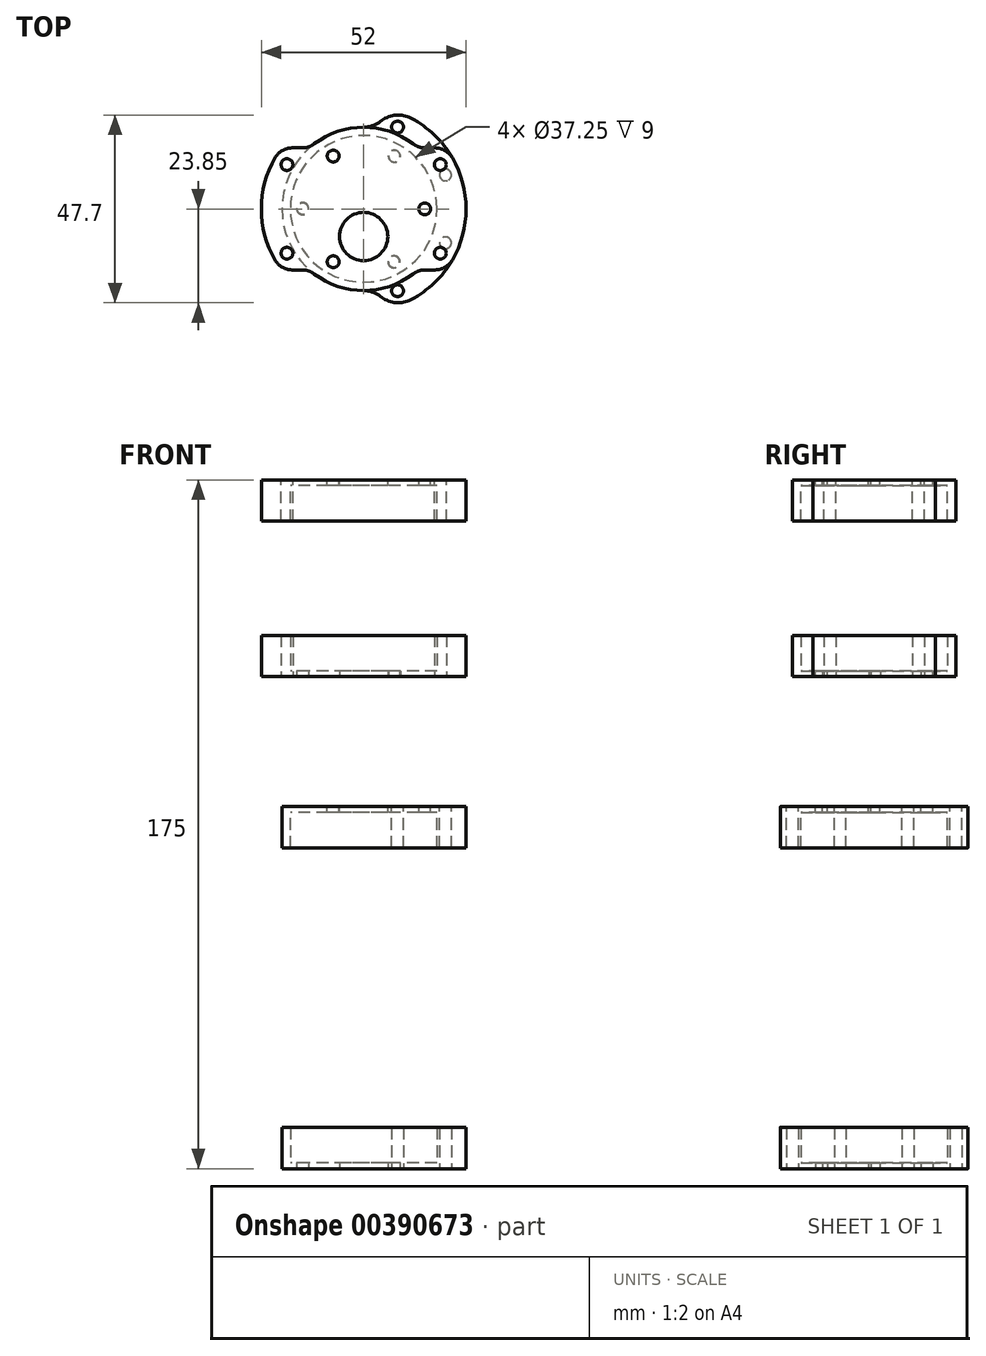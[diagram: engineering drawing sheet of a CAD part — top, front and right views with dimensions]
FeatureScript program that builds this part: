
annotation { "Feature Type Name" : "Feature", "Feature Type Description" : "" }
export const myFeature = defineFeature(function(context is Context, id is Id, definition is map)
    precondition{}
    {
        {
            var Q0;
            Q0=qCreatedBy(makeId("Top.planeOp"),FACE);
            cPlane(context, id + "F0", {"entities" : qUnion([Q0]), "cplaneType" : CPlaneType.OFFSET, "offset" : 92 * mm, "width" : 150 * mm, "height" : 150 * mm});
        }
        {
            var Q0;
            Q0=qCreatedBy(makeId("Top.planeOp"),FACE);
            var sketch = newSketch(context, id + "F1", { "sketchPlane" : qUnion([Q0])});
            skCircle(sketch, "E0", {"center": v(0, 0) * mm, "radius": 18.62 * mm});
            skCircle(sketch, "E1", {"center": v(0, 0) * mm, "radius": 26 * mm});
            skCircle(sketch, "E2", {"center": v(0, -7) * mm, "radius": 6.12 * mm});
            skCircle(sketch, "E3", {"center": v(0, 0) * mm, "radius": 15.5 * mm, "construction": true});
            skCircle(sketch, "E4", {"center": v(-15.5, 0) * mm, "radius": 1.5 * mm});
            skCircle(sketch, "E5.1.0", {"center": v(7.75, -13.42) * mm, "radius": 1.5 * mm});
            skCircle(sketch, "E5.2.0", {"center": v(7.75, 13.42) * mm, "radius": 1.5 * mm});
            skCircle(sketch, "E6", {"center": v(-20.79, 8.61) * mm, "radius": 1.5 * mm});
            skLineSegment(sketch, "E7", {"start": v(-20.79, 8.61) * mm, "end": v(0, 0) * mm, "construction": true});
            skCircle(sketch, "E8.1.0", {"center": v(-20.79, -8.61) * mm, "radius": 1.5 * mm});
            skCircle(sketch, "E8.2.0", {"center": v(-8.61, -20.79) * mm, "radius": 1.5 * mm});
            skCircle(sketch, "E8.3.0", {"center": v(8.61, -20.79) * mm, "radius": 1.5 * mm});
            skCircle(sketch, "E8.4.0", {"center": v(20.79, -8.61) * mm, "radius": 1.5 * mm});
            skCircle(sketch, "E8.5.0", {"center": v(20.79, 8.61) * mm, "radius": 1.5 * mm});
            skCircle(sketch, "E9", {"center": v(0, 0) * mm, "radius": 20.75 * mm});
            skLineSegment(sketch, "E10", {"start": v(0, 20.75) * mm, "end": v(0, 26) * mm});
            skLineSegment(sketch, "E11", {"start": v(0, -20.75) * mm, "end": v(0, -26) * mm});
            skCircle(sketch, "E12.1.6.0", {"center": v(8.61, 20.79) * mm, "radius": 1.5 * mm});
            skCircle(sketch, "E12.1.7.0", {"center": v(-8.61, 20.79) * mm, "radius": 1.5 * mm});
            skSolve(sketch);
        }
        {
            var Q0;
            Q0=qCreatedBy(id+"F0.planeOp",FACE);
            var sketch = newSketch(context, id + "F2", { "sketchPlane" : qUnion([Q0])});
            skCircle(sketch, "E13", {"center": v(0, 0) * mm, "radius": 18.62 * mm});
            skCircle(sketch, "E14", {"center": v(0, 0) * mm, "radius": 26 * mm});
            skCircle(sketch, "E15", {"center": v(0, -7) * mm, "radius": 6.12 * mm});
            skCircle(sketch, "E16", {"center": v(0, 0) * mm, "radius": 15.5 * mm, "construction": true});
            skCircle(sketch, "E17", {"center": v(-20.79, 8.61) * mm, "radius": 1.5 * mm});
            skLineSegment(sketch, "E18", {"start": v(-20.79, 8.61) * mm, "end": v(0, 0) * mm, "construction": true});
            skCircle(sketch, "E19.1.0", {"center": v(-20.79, -8.61) * mm, "radius": 1.5 * mm});
            skCircle(sketch, "E19.2.0", {"center": v(-8.61, -20.79) * mm, "radius": 1.5 * mm});
            skCircle(sketch, "E19.3.0", {"center": v(8.61, -20.79) * mm, "radius": 1.5 * mm});
            skCircle(sketch, "E19.4.0", {"center": v(20.79, -8.61) * mm, "radius": 1.5 * mm});
            skCircle(sketch, "E19.5.0", {"center": v(20.79, 8.61) * mm, "radius": 1.5 * mm});
            skCircle(sketch, "E20", {"center": v(0, 0) * mm, "radius": 20.75 * mm});
            skLineSegment(sketch, "E21", {"start": v(0, 20.75) * mm, "end": v(0, 26) * mm});
            skLineSegment(sketch, "E22", {"start": v(0, -20.75) * mm, "end": v(0, -26) * mm});
            skCircle(sketch, "E23.1.6.0", {"center": v(8.61, 20.79) * mm, "radius": 1.5 * mm});
            skCircle(sketch, "E23.1.7.0", {"center": v(-8.61, 20.79) * mm, "radius": 1.5 * mm});
            skCircle(sketch, "E24", {"center": v(15.5, 0) * mm, "radius": 1.5 * mm});
            skCircle(sketch, "E25.1.0", {"center": v(-7.75, 13.42) * mm, "radius": 1.5 * mm});
            skCircle(sketch, "E25.2.0", {"center": v(-7.75, -13.42) * mm, "radius": 1.5 * mm});
            skSolve(sketch);
        }
        {
            var Q0;
            Q0=makeQuery(id+"F1.imprint","IMPRINT",FACE,{"disambiguationData":[TD([[makeQuery(id+"F1.imprint","IMPRINT",EDGE,{"derivedFrom":sQuery(id+"F1.wireOp",EDGE,"E0")}),1.0]])]});
            extrude(context, id + "F3", {"entities" : qUnion([Q0]), "depth" : 1.5 * mm});
        }
        {
            var Q0;
            Q0=makeQuery(id+"F2.imprint","IMPRINT",FACE,{"disambiguationData":[TD([[makeQuery(id+"F2.imprint","IMPRINT",EDGE,{"derivedFrom":sQuery(id+"F2.wireOp",EDGE,"E13")}),1.0]])]});
            extrude(context, id + "F4", {"entities" : qUnion([Q0]), "oppositeDirection" : true, "depth" : 1.5 * mm});
        }
        {
            var Q0;
            Q0=makeQuery(id+"F1.imprint","IMPRINT",FACE,{"disambiguationData":[TD([[makeQuery(id+"F1.imprint","IMPRINT",EDGE,{"derivedFrom":sQuery(id+"F1.wireOp",EDGE,"E0")}),-1.0]])]});
            var Q1;
            Q1=makeQuery(id+"F1.imprint","IMPRINT",FACE,{"disambiguationData":[TD([[makeQuery(id+"F1.imprint","IMPRINT",EDGE,{"derivedFrom":sQuery(id+"F1.wireOp",EDGE,"E8.3.0")}),-1.0]])]});
            extrude(context, id + "F5", {"entities" : qUnion([Q0, Q1]), "operationType" : NewBodyOperationType.ADD, "depth" : 10.5 * mm});
        }
        {
            var Q0;
            Q0=makeQuery(id+"F2.imprint","IMPRINT",FACE,{"disambiguationData":[TD([[makeQuery(id+"F2.imprint","IMPRINT",EDGE,{"derivedFrom":sQuery(id+"F2.wireOp",EDGE,"E13")}),-1.0]])]});
            var Q1;
            Q1=makeQuery(id+"F2.imprint","IMPRINT",FACE,{"disambiguationData":[TD([[makeQuery(id+"F2.imprint","IMPRINT",EDGE,{"derivedFrom":sQuery(id+"F2.wireOp",EDGE,"E19.3.0")}),-1.0]])]});
            extrude(context, id + "F6", {"entities" : qUnion([Q0, Q1]), "operationType" : NewBodyOperationType.ADD, "oppositeDirection" : true, "depth" : 10.5 * mm});
        }
        {
            var Q0;
            Q0=makeQuery(id+"F5.opExtrude","SWEPT_EDGE",EDGE,{"disambiguationData":[OSD([sQuery(id+"F1.wireOp",EDGE,"E1"),sQuery(id+"F1.wireOp",EDGE,"E10")])]});
            var Q1;
            Q1=makeQuery(id+"F5.opExtrude","SWEPT_EDGE",EDGE,{"disambiguationData":[OSD([sQuery(id+"F1.wireOp",EDGE,"E1"),sQuery(id+"F1.wireOp",EDGE,"E11")])]});
            var Q2;
            Q2=makeQuery(id+"F5.opExtrude","SWEPT_EDGE",EDGE,{"disambiguationData":[OSD([sQuery(id+"F2.wireOp",EDGE,"E14"),sQuery(id+"F2.wireOp",EDGE,"E22")])]});
            var Q3;
            Q3=makeQuery(id+"F5.opExtrude","SWEPT_EDGE",EDGE,{"disambiguationData":[OSD([sQuery(id+"F2.wireOp",EDGE,"E14"),sQuery(id+"F2.wireOp",EDGE,"E21")])]});
            var Q4;
            Q4=makeQuery(id+"F6.opExtrude","SWEPT_EDGE",EDGE,{"disambiguationData":[OSD([sQuery(id+"F2.wireOp",EDGE,"E14"),sQuery(id+"F2.wireOp",EDGE,"E21")])]});
            var Q5;
            Q5=makeQuery(id+"F6.opExtrude","SWEPT_EDGE",EDGE,{"disambiguationData":[OSD([sQuery(id+"F2.wireOp",EDGE,"E14"),sQuery(id+"F2.wireOp",EDGE,"E22")])]});
            chamfer(context, id + "F7", {"entities" : qUnion([Q0, Q1, Q2, Q3, Q4, Q5]), "width" : 6 * mm, "tangentPropagation" : true});
        }
        {
            var Q0;
            Q0=makeQuery(id+"F7.opChamfer","BLEND_EDGE",EDGE,{"blendedFrom":[makeQuery(id+"F5.opExtrude","SWEPT_EDGE",EDGE,{"disambiguationData":[OSD([sQuery(id+"F1.wireOp",EDGE,"E1"),sQuery(id+"F1.wireOp",EDGE,"E11")])]}),makeQuery(id+"F5.opExtrude","SWEPT_FACE",FACE,{"disambiguationData":[OSD([sQuery(id+"F1.wireOp",EDGE,"E9")])]})],"blendedInto":[makeQuery(id+"F5.opExtrude","SWEPT_FACE",FACE,{"disambiguationData":[OSD([sQuery(id+"F1.wireOp",EDGE,"E9")])]})]});
            var Q1;
            Q1=makeQuery(id+"F7.opChamfer","BLEND_EDGE",EDGE,{"blendedFrom":[makeQuery(id+"F5.opExtrude","SWEPT_EDGE",EDGE,{"disambiguationData":[OSD([sQuery(id+"F1.wireOp",EDGE,"E1"),sQuery(id+"F1.wireOp",EDGE,"E10")])]}),makeQuery(id+"F5.opExtrude","SWEPT_FACE",FACE,{"disambiguationData":[OSD([sQuery(id+"F1.wireOp",EDGE,"E9")])]})],"blendedInto":[makeQuery(id+"F5.opExtrude","SWEPT_FACE",FACE,{"disambiguationData":[OSD([sQuery(id+"F1.wireOp",EDGE,"E9")])]})]});
            var Q2;
            {var subQ0=sQuery(id+"F1.wireOp",EDGE,"E1");Q2=makeQuery(id+"F7.opChamfer","BLEND_EDGE",EDGE,{"blendedFrom":[makeQuery(id+"F5.opExtrude","SWEPT_EDGE",EDGE,{"disambiguationData":[OSD([subQ0,sQuery(id+"F1.wireOp",EDGE,"E10")])]}),makeQuery(id+"F5.opExtrude","SWEPT_FACE",FACE,{"disambiguationData":[OSD([subQ0])]})],"blendedInto":[makeQuery(id+"F5.opExtrude","SWEPT_FACE",FACE,{"disambiguationData":[OSD([subQ0])]})]});}
            var Q3;
            {var subQ0=sQuery(id+"F1.wireOp",EDGE,"E1");Q3=makeQuery(id+"F7.opChamfer","BLEND_EDGE",EDGE,{"blendedFrom":[makeQuery(id+"F5.opExtrude","SWEPT_EDGE",EDGE,{"disambiguationData":[OSD([subQ0,sQuery(id+"F1.wireOp",EDGE,"E11")])]}),makeQuery(id+"F5.opExtrude","SWEPT_FACE",FACE,{"disambiguationData":[OSD([subQ0])]})],"blendedInto":[makeQuery(id+"F5.opExtrude","SWEPT_FACE",FACE,{"disambiguationData":[OSD([subQ0])]})]});}
            var Q4;
            {var subQ0=sQuery(id+"F2.wireOp",EDGE,"E14");Q4=makeQuery(id+"F7.opChamfer","BLEND_EDGE",EDGE,{"blendedFrom":[makeQuery(id+"F5.opExtrude","SWEPT_EDGE",EDGE,{"disambiguationData":[OSD([subQ0,sQuery(id+"F2.wireOp",EDGE,"E21")])]}),makeQuery(id+"F5.opExtrude","SWEPT_FACE",FACE,{"disambiguationData":[OSD([subQ0])]})],"blendedInto":[makeQuery(id+"F5.opExtrude","SWEPT_FACE",FACE,{"disambiguationData":[OSD([subQ0])]})]});}
            var Q5;
            Q5=makeQuery(id+"F7.opChamfer","BLEND_EDGE",EDGE,{"blendedFrom":[makeQuery(id+"F5.opExtrude","SWEPT_EDGE",EDGE,{"disambiguationData":[OSD([sQuery(id+"F2.wireOp",EDGE,"E14"),sQuery(id+"F2.wireOp",EDGE,"E21")])]}),makeQuery(id+"F5.opExtrude","SWEPT_FACE",FACE,{"disambiguationData":[OSD([sQuery(id+"F2.wireOp",EDGE,"E20")])]})],"blendedInto":[makeQuery(id+"F5.opExtrude","SWEPT_FACE",FACE,{"disambiguationData":[OSD([sQuery(id+"F2.wireOp",EDGE,"E20")])]})]});
            var Q6;
            Q6=makeQuery(id+"F7.opChamfer","BLEND_EDGE",EDGE,{"blendedFrom":[makeQuery(id+"F5.opExtrude","SWEPT_EDGE",EDGE,{"disambiguationData":[OSD([sQuery(id+"F2.wireOp",EDGE,"E14"),sQuery(id+"F2.wireOp",EDGE,"E22")])]}),makeQuery(id+"F5.opExtrude","SWEPT_FACE",FACE,{"disambiguationData":[OSD([sQuery(id+"F2.wireOp",EDGE,"E20")])]})],"blendedInto":[makeQuery(id+"F5.opExtrude","SWEPT_FACE",FACE,{"disambiguationData":[OSD([sQuery(id+"F2.wireOp",EDGE,"E20")])]})]});
            var Q7;
            {var subQ0=sQuery(id+"F2.wireOp",EDGE,"E14");Q7=makeQuery(id+"F7.opChamfer","BLEND_EDGE",EDGE,{"blendedFrom":[makeQuery(id+"F5.opExtrude","SWEPT_EDGE",EDGE,{"disambiguationData":[OSD([subQ0,sQuery(id+"F2.wireOp",EDGE,"E22")])]}),makeQuery(id+"F5.opExtrude","SWEPT_FACE",FACE,{"disambiguationData":[OSD([subQ0])]})],"blendedInto":[makeQuery(id+"F5.opExtrude","SWEPT_FACE",FACE,{"disambiguationData":[OSD([subQ0])]})]});}
            var Q8;
            {var subQ0=sQuery(id+"F2.wireOp",EDGE,"E14");Q8=makeQuery(id+"F7.opChamfer","BLEND_EDGE",EDGE,{"blendedFrom":[makeQuery(id+"F6.opExtrude","SWEPT_EDGE",EDGE,{"disambiguationData":[OSD([subQ0,sQuery(id+"F2.wireOp",EDGE,"E22")])]}),makeQuery(id+"F6.opExtrude","SWEPT_FACE",FACE,{"disambiguationData":[OSD([subQ0])]})],"blendedInto":[makeQuery(id+"F6.opExtrude","SWEPT_FACE",FACE,{"disambiguationData":[OSD([subQ0])]})]});}
            var Q9;
            Q9=makeQuery(id+"F7.opChamfer","BLEND_EDGE",EDGE,{"blendedFrom":[makeQuery(id+"F6.opExtrude","SWEPT_EDGE",EDGE,{"disambiguationData":[OSD([sQuery(id+"F2.wireOp",EDGE,"E14"),sQuery(id+"F2.wireOp",EDGE,"E22")])]}),makeQuery(id+"F6.opExtrude","SWEPT_FACE",FACE,{"disambiguationData":[OSD([sQuery(id+"F2.wireOp",EDGE,"E20")])]})],"blendedInto":[makeQuery(id+"F6.opExtrude","SWEPT_FACE",FACE,{"disambiguationData":[OSD([sQuery(id+"F2.wireOp",EDGE,"E20")])]})]});
            var Q10;
            Q10=makeQuery(id+"F7.opChamfer","BLEND_EDGE",EDGE,{"blendedFrom":[makeQuery(id+"F6.opExtrude","SWEPT_EDGE",EDGE,{"disambiguationData":[OSD([sQuery(id+"F2.wireOp",EDGE,"E14"),sQuery(id+"F2.wireOp",EDGE,"E21")])]}),makeQuery(id+"F6.opExtrude","SWEPT_FACE",FACE,{"disambiguationData":[OSD([sQuery(id+"F2.wireOp",EDGE,"E20")])]})],"blendedInto":[makeQuery(id+"F6.opExtrude","SWEPT_FACE",FACE,{"disambiguationData":[OSD([sQuery(id+"F2.wireOp",EDGE,"E20")])]})]});
            var Q11;
            {var subQ0=sQuery(id+"F2.wireOp",EDGE,"E14");Q11=makeQuery(id+"F7.opChamfer","BLEND_EDGE",EDGE,{"blendedFrom":[makeQuery(id+"F6.opExtrude","SWEPT_EDGE",EDGE,{"disambiguationData":[OSD([subQ0,sQuery(id+"F2.wireOp",EDGE,"E21")])]}),makeQuery(id+"F6.opExtrude","SWEPT_FACE",FACE,{"disambiguationData":[OSD([subQ0])]})],"blendedInto":[makeQuery(id+"F6.opExtrude","SWEPT_FACE",FACE,{"disambiguationData":[OSD([subQ0])]})]});}
            fillet(context, id + "F8", {"entities" : qUnion([Q0, Q1, Q2, Q3, Q4, Q5, Q6, Q7, Q8, Q9, Q10, Q11]), "radius" : 7 * mm, "tangentPropagation" : true, "allowEdgeOverflow" : false});
        }
        {
            var Q0;
            Q0=qCreatedBy(makeId("Top.planeOp"),FACE);
            cPlane(context, id + "F9", {"entities" : qUnion([Q0]), "cplaneType" : CPlaneType.OFFSET, "offset" : 125 * mm, "width" : 150 * mm, "height" : 150 * mm});
        }
        {
            var Q0;
            Q0=qCreatedBy(id+"F9.planeOp",FACE);
            cPlane(context, id + "F10", {"entities" : qUnion([Q0]), "cplaneType" : CPlaneType.OFFSET, "offset" : 50 * mm, "width" : 150 * mm, "height" : 150 * mm});
        }
        {
            var Q0;
            Q0=qCreatedBy(id+"F9.planeOp",FACE);
            var sketch = newSketch(context, id + "F11", { "sketchPlane" : qUnion([Q0])});
            skCircle(sketch, "E26", {"center": v(0, 0) * mm, "radius": 18.62 * mm});
            skCircle(sketch, "E27", {"center": v(0, 0) * mm, "radius": 26 * mm});
            skCircle(sketch, "E28", {"center": v(0, -7) * mm, "radius": 6.12 * mm});
            skCircle(sketch, "E29", {"center": v(0, 0) * mm, "radius": 15.5 * mm, "construction": true});
            skCircle(sketch, "E30", {"center": v(-15.5, 0.12) * mm, "radius": 1.5 * mm});
            skCircle(sketch, "E31.1.0", {"center": v(7.65, -13.48) * mm, "radius": 1.5 * mm});
            skCircle(sketch, "E31.2.0", {"center": v(7.85, 13.36) * mm, "radius": 1.5 * mm});
            skCircle(sketch, "E32", {"center": v(-19.49, 11.25) * mm, "radius": 1.5 * mm});
            skLineSegment(sketch, "E33", {"start": v(-19.49, 11.25) * mm, "end": v(0, 0) * mm, "construction": true});
            skCircle(sketch, "E34.1.0", {"center": v(-19.49, -11.25) * mm, "radius": 1.5 * mm});
            skCircle(sketch, "E34.2.0", {"center": v(0, -22.5) * mm, "radius": 1.5 * mm});
            skCircle(sketch, "E34.3.0", {"center": v(19.49, -11.25) * mm, "radius": 1.5 * mm});
            skCircle(sketch, "E34.4.0", {"center": v(19.49, 11.25) * mm, "radius": 1.5 * mm});
            skCircle(sketch, "E34.5.0", {"center": v(0, 22.5) * mm, "radius": 1.5 * mm});
            skCircle(sketch, "E35", {"center": v(0, 0) * mm, "radius": 20.75 * mm});
            skLineSegment(sketch, "E36", {"start": v(20.87, -15.5) * mm, "end": v(13.8, -15.5) * mm});
            skLineSegment(sketch, "E37.MirrorCS", {"start": v(-20.87, -15.5) * mm, "end": v(-13.8, -15.5) * mm});
            skLineSegment(sketch, "E38.MirrorCS", {"start": v(20.87, 15.5) * mm, "end": v(13.8, 15.5) * mm});
            skLineSegment(sketch, "E39.MirrorCS", {"start": v(-20.87, 15.5) * mm, "end": v(-13.8, 15.5) * mm});
            skSolve(sketch);
        }
        {
            var Q0;
            Q0=qCreatedBy(id+"F10.planeOp",FACE);
            var sketch = newSketch(context, id + "F12", { "sketchPlane" : qUnion([Q0])});
            skCircle(sketch, "E40", {"center": v(0, 0) * mm, "radius": 18.62 * mm});
            skCircle(sketch, "E41", {"center": v(0, 0) * mm, "radius": 26 * mm});
            skCircle(sketch, "E42", {"center": v(0, -7) * mm, "radius": 6.12 * mm});
            skCircle(sketch, "E43", {"center": v(0, 0) * mm, "radius": 15.5 * mm, "construction": true});
            skCircle(sketch, "E44", {"center": v(0, 0) * mm, "radius": 20.75 * mm});
            skLineSegment(sketch, "E45", {"start": v(20.87, -15.5) * mm, "end": v(13.8, -15.5) * mm});
            skLineSegment(sketch, "E46.MirrorCS", {"start": v(-20.87, -15.5) * mm, "end": v(-13.8, -15.5) * mm});
            skLineSegment(sketch, "E47.MirrorCS", {"start": v(-20.87, 15.5) * mm, "end": v(-13.8, 15.5) * mm});
            skLineSegment(sketch, "E48.MirrorCS", {"start": v(20.87, 15.5) * mm, "end": v(13.8, 15.5) * mm});
            skCircle(sketch, "E49", {"center": v(15.5, 0) * mm, "radius": 1.5 * mm});
            skCircle(sketch, "E50.1.0", {"center": v(-7.75, 13.42) * mm, "radius": 1.5 * mm});
            skCircle(sketch, "E50.2.0", {"center": v(-7.75, -13.42) * mm, "radius": 1.5 * mm});
            skCircle(sketch, "E51", {"center": v(-19.49, 11.25) * mm, "radius": 1.5 * mm});
            skLineSegment(sketch, "E52", {"start": v(-19.49, 11.25) * mm, "end": v(0, 0) * mm, "construction": true});
            skCircle(sketch, "E53.1.0", {"center": v(-19.49, -11.25) * mm, "radius": 1.5 * mm});
            skCircle(sketch, "E53.2.0", {"center": v(0, -22.5) * mm, "radius": 1.5 * mm});
            skCircle(sketch, "E53.3.0", {"center": v(19.49, -11.25) * mm, "radius": 1.5 * mm});
            skCircle(sketch, "E53.4.0", {"center": v(19.49, 11.25) * mm, "radius": 1.5 * mm});
            skCircle(sketch, "E53.5.0", {"center": v(0, 22.5) * mm, "radius": 1.5 * mm});
            skSolve(sketch);
        }
        {
            var Q0;
            Q0=makeQuery(id+"F11.imprint","IMPRINT",FACE,{"disambiguationData":[TD([[makeQuery(id+"F11.imprint","IMPRINT",EDGE,{"derivedFrom":sQuery(id+"F11.wireOp",EDGE,"E26")}),1.0]])]});
            extrude(context, id + "F13", {"entities" : qUnion([Q0]), "depth" : 1.5 * mm});
        }
        {
            var Q0;
            Q0=makeQuery(id+"F11.imprint","IMPRINT",FACE,{"disambiguationData":[TD([[makeQuery(id+"F11.imprint","IMPRINT",EDGE,{"derivedFrom":sQuery(id+"F11.wireOp",EDGE,"E32")}),-1.0]])]});
            var Q1;
            Q1=makeQuery(id+"F11.imprint","IMPRINT",FACE,{"disambiguationData":[TD([[makeQuery(id+"F11.imprint","IMPRINT",EDGE,{"derivedFrom":sQuery(id+"F11.wireOp",EDGE,"E26")}),-1.0]])]});
            var Q2;
            Q2=makeQuery(id+"F11.imprint","IMPRINT",FACE,{"disambiguationData":[TD([[makeQuery(id+"F11.imprint","IMPRINT",EDGE,{"derivedFrom":sQuery(id+"F11.wireOp",EDGE,"E34.3.0")}),-1.0]])]});
            extrude(context, id + "F14", {"entities" : qUnion([Q0, Q1, Q2]), "operationType" : NewBodyOperationType.ADD, "depth" : 10.5 * mm});
        }
        {
            var Q0;
            Q0=makeQuery(id+"F12.imprint","IMPRINT",FACE,{"disambiguationData":[TD([[makeQuery(id+"F12.imprint","IMPRINT",EDGE,{"derivedFrom":sQuery(id+"F12.wireOp",EDGE,"E40")}),1.0]])]});
            extrude(context, id + "F15", {"entities" : qUnion([Q0]), "oppositeDirection" : true, "depth" : 1.5 * mm});
        }
        {
            var Q0;
            {var subQ1=sQuery(id+"F12.wireOp",EDGE,"E45");Q0=makeQuery(id+"F12.imprint","IMPRINT",FACE,{"disambiguationData":[TD([[makeQuery(id+"F12.imprint","IMPRINT",EDGE,{"derivedFrom":subQ1}),-1.0]])]});}
            var Q1;
            Q1=makeQuery(id+"F12.imprint","IMPRINT",FACE,{"disambiguationData":[TD([[makeQuery(id+"F12.imprint","IMPRINT",EDGE,{"derivedFrom":sQuery(id+"F12.wireOp",EDGE,"E40")}),-1.0]])]});
            var Q2;
            {var subQ0=sQuery(id+"F12.wireOp",EDGE,"E46.MirrorCS");Q2=makeQuery(id+"F12.imprint","IMPRINT",FACE,{"disambiguationData":[TD([[makeQuery(id+"F12.imprint","IMPRINT",EDGE,{"derivedFrom":subQ0}),1.0]])]});}
            extrude(context, id + "F16", {"entities" : qUnion([Q0, Q1, Q2]), "operationType" : NewBodyOperationType.ADD, "oppositeDirection" : true, "depth" : 10.5 * mm});
        }
        {
            var Q0;
            Q0=makeQuery(id+"F14.opExtrude","SWEPT_EDGE",EDGE,{"disambiguationData":[OSD([sQuery(id+"F11.wireOp",EDGE,"E27"),sQuery(id+"F11.wireOp",EDGE,"EbLUmnxA-kGfZ-o2ID-BWPR-tWaErnmTWbPK")])]});
            var Q1;
            Q1=makeQuery(id+"F14.opExtrude","SWEPT_EDGE",EDGE,{"disambiguationData":[OSD([sQuery(id+"F11.wireOp",EDGE,"E35"),sQuery(id+"F11.wireOp",EDGE,"EbLUmnxA-kGfZ-o2ID-BWPR-tWaErnmTWbPK")])]});
            var Q2;
            Q2=makeQuery(id+"F14.opExtrude","SWEPT_EDGE",EDGE,{"disambiguationData":[OSD([sQuery(id+"F11.wireOp",EDGE,"E27"),sQuery(id+"F11.wireOp",EDGE,"KzaSrYpL-XU7z-rx1D-WPNd-F9J1fatBlVJU")])]});
            var Q3;
            Q3=makeQuery(id+"F14.opExtrude","SWEPT_EDGE",EDGE,{"disambiguationData":[OSD([sQuery(id+"F11.wireOp",EDGE,"E35"),sQuery(id+"F11.wireOp",EDGE,"KzaSrYpL-XU7z-rx1D-WPNd-F9J1fatBlVJU")])]});
            var Q4;
            Q4=makeQuery(id+"F16.opExtrude","SWEPT_EDGE",EDGE,{"disambiguationData":[OSD([sQuery(id+"F12.wireOp",EDGE,"E44"),sQuery(id+"F12.wireOp",EDGE,"E47.MirrorCS")])]});
            var Q5;
            Q5=makeQuery(id+"F16.opExtrude","SWEPT_EDGE",EDGE,{"disambiguationData":[OSD([sQuery(id+"F12.wireOp",EDGE,"E41"),sQuery(id+"F12.wireOp",EDGE,"E47.MirrorCS")])]});
            var Q6;
            Q6=makeQuery(id+"F16.opExtrude","SWEPT_EDGE",EDGE,{"disambiguationData":[OSD([sQuery(id+"F12.wireOp",EDGE,"E44"),sQuery(id+"F12.wireOp",EDGE,"E48.MirrorCS")])]});
            var Q7;
            Q7=makeQuery(id+"F16.opExtrude","SWEPT_EDGE",EDGE,{"disambiguationData":[OSD([sQuery(id+"F12.wireOp",EDGE,"E41"),sQuery(id+"F12.wireOp",EDGE,"E48.MirrorCS")])]});
            var Q8;
            Q8=makeQuery(id+"F16.opExtrude","SWEPT_EDGE",EDGE,{"disambiguationData":[OSD([sQuery(id+"F12.wireOp",EDGE,"E41"),sQuery(id+"F12.wireOp",EDGE,"E45")])]});
            var Q9;
            Q9=makeQuery(id+"F16.opExtrude","SWEPT_EDGE",EDGE,{"disambiguationData":[OSD([sQuery(id+"F12.wireOp",EDGE,"E44"),sQuery(id+"F12.wireOp",EDGE,"E45")])]});
            var Q10;
            Q10=makeQuery(id+"F16.opExtrude","SWEPT_EDGE",EDGE,{"disambiguationData":[OSD([sQuery(id+"F12.wireOp",EDGE,"E44"),sQuery(id+"F12.wireOp",EDGE,"E46.MirrorCS")])]});
            var Q11;
            Q11=makeQuery(id+"F16.opExtrude","SWEPT_EDGE",EDGE,{"disambiguationData":[OSD([sQuery(id+"F12.wireOp",EDGE,"E41"),sQuery(id+"F12.wireOp",EDGE,"E46.MirrorCS")])]});
            fillet(context, id + "F17", {"entities" : qUnion([Q0, Q1, Q2, Q3, Q4, Q5, Q6, Q7, Q8, Q9, Q10, Q11]), "radius" : 5 * mm, "tangentPropagation" : true, "allowEdgeOverflow" : false});
        }
    });
